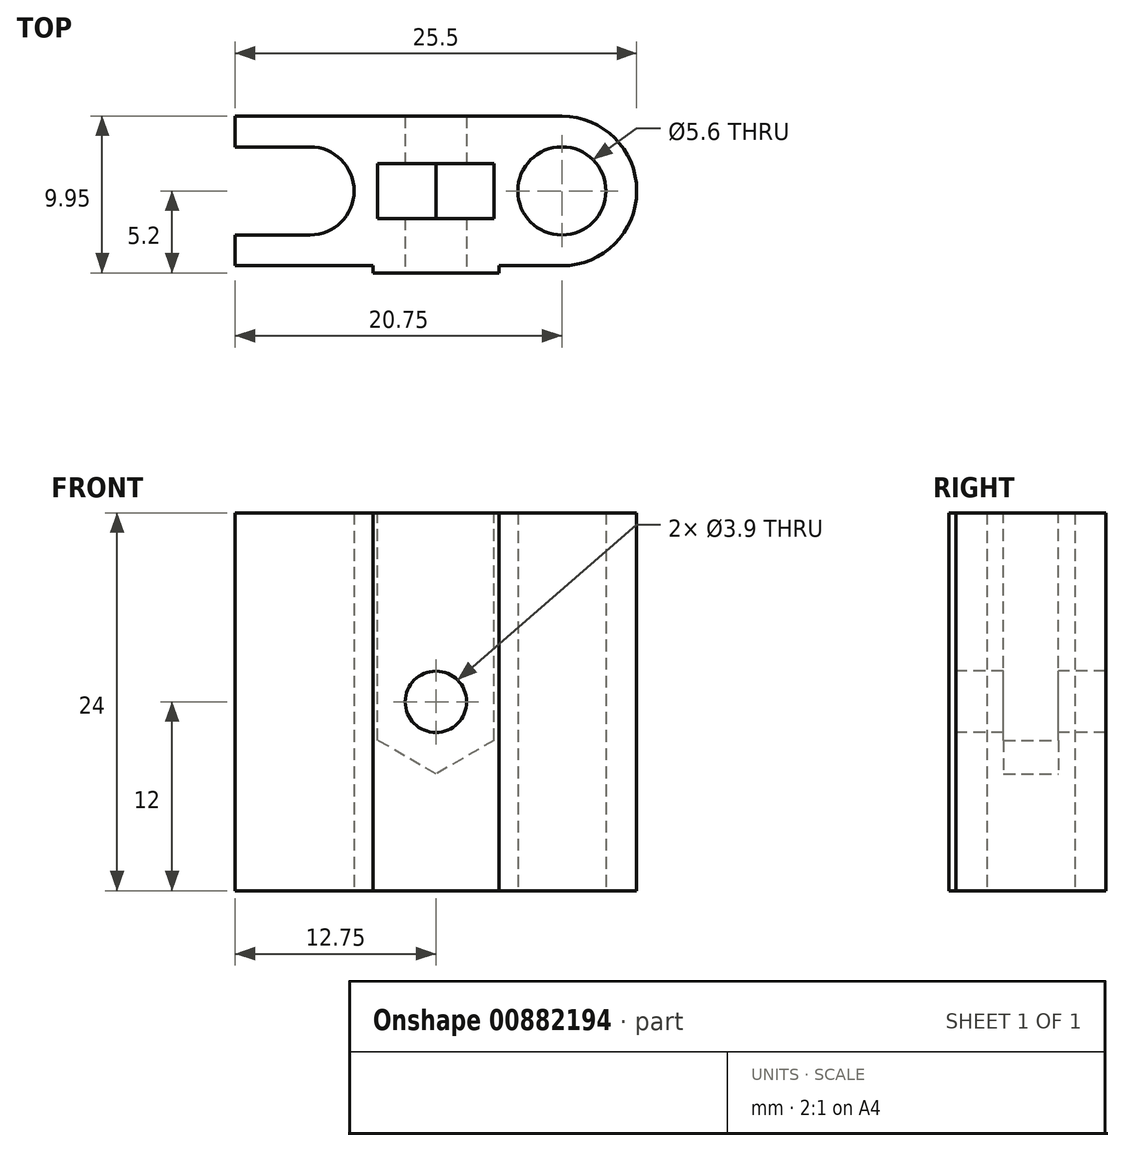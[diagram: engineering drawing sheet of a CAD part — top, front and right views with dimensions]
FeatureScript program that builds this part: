
annotation { "Feature Type Name" : "Feature", "Feature Type Description" : "" }
export const myFeature = defineFeature(function(context is Context, id is Id, definition is map)
    precondition{}
    {
        {
            var Q0;
            Q0=qCreatedBy(makeId("Top.planeOp"),FACE);
            var sketch = newSketch(context, id + "F0", { "sketchPlane" : qUnion([Q0])});
            skLineSegment(sketch, "E0", {"start": v(-8, 0) * mm, "end": v(8, 0) * mm, "construction": true});
            skArc(sketch, "E1", {"start": v(-8, -2.8) * mm, "mid": v(-5.2, 0) * mm, "end": v(-8, 2.8) * mm});
            skLineSegment(sketch, "E2", {"start": v(0, 21.05) * mm, "end": v(0, -24.42) * mm, "construction": true});
            skCircle(sketch, "E3.MirrorC", {"center": v(8, 0) * mm, "radius": 2.8 * mm});
            skLineSegment(sketch, "E4.bottom", {"start": v(8, 4.75) * mm, "end": v(-8, 4.75) * mm});
            skLineSegment(sketch, "E4.top", {"start": v(8, -4.75) * mm, "end": v(-8, -4.75) * mm});
            skLineSegment(sketch, "E4.left", {"start": v(8, 4.75) * mm, "end": v(8, -4.75) * mm, "construction": true});
            skPoint(sketch, "E4.middle", {"position": v(0, 0) * mm});
            skArc(sketch, "E5.0", {"start": v(8, 4.75) * mm, "mid": v(12.75, 0) * mm, "end": v(8, -4.75) * mm});
            skLineSegment(sketch, "E6.bottom", {"start": v(-8, 4.75) * mm, "end": v(-12.75, 4.75) * mm});
            skLineSegment(sketch, "E6.top", {"start": v(-8, -4.75) * mm, "end": v(-12.75, -4.75) * mm});
            skLineSegment(sketch, "E6.left", {"start": v(-8, 4.75) * mm, "end": v(-8, -4.75) * mm, "construction": true});
            skLineSegment(sketch, "E6.right", {"start": v(-12.75, 4.75) * mm, "end": v(-12.75, 2.8) * mm});
            skLineSegment(sketch, "E7", {"start": v(-8, 2.8) * mm, "end": v(-12.75, 2.8) * mm});
            skLineSegment(sketch, "E8", {"start": v(-8, -2.8) * mm, "end": v(-12.75, -2.8) * mm});
            skLineSegment(sketch, "E9.trimOffspring", {"start": v(-12.75, -2.8) * mm, "end": v(-12.75, -4.75) * mm});
            skLineSegment(sketch, "E10.bottom", {"start": v(4, -4.3) * mm, "end": v(-4, -4.3) * mm});
            skLineSegment(sketch, "E10.top", {"start": v(4, -5.2) * mm, "end": v(-4, -5.2) * mm});
            skLineSegment(sketch, "E10.left", {"start": v(4, -4.3) * mm, "end": v(4, -5.2) * mm});
            skLineSegment(sketch, "E10.right", {"start": v(-4, -4.3) * mm, "end": v(-4, -5.2) * mm});
            skPoint(sketch, "E10.middle", {"position": v(0, -4.75) * mm});
            skSolve(sketch);
        }
        {
            var Q0;
            Q0=qSketchRegion(id+"F0",true);
            var Q1;
            Q1=qSketchRegion(id+"F2",true);
            extrude(context, id + "F1", {"entities" : qUnion([Q0, Q1]), "depth" : 24 * mm, "offsetDistance" : 25 * mm});
        }
        {
            var Q0;
            Q0=makeQuery(id+"F1.opExtrude","SWEPT_FACE",FACE,{"disambiguationData":[OSD([sQuery(id+"F0.wireOp",EDGE,"E10.top")])]});
            var sketch = newSketch(context, id + "F2", { "sketchPlane" : qUnion([Q0])});
            skLineSegment(sketch, "E11.bottom", {"start": v(-4, 24) * mm, "end": v(4, 24) * mm, "construction": true});
            skLineSegment(sketch, "E11.top", {"start": v(-4, 0) * mm, "end": v(4, 0) * mm, "construction": true});
            skLineSegment(sketch, "E11.left", {"start": v(-4, 24) * mm, "end": v(-4, 0) * mm, "construction": true});
            skLineSegment(sketch, "E11.right", {"start": v(4, 24) * mm, "end": v(4, 0) * mm, "construction": true});
            skLineSegment(sketch, "E12", {"start": v(-4, 24) * mm, "end": v(4, 0) * mm, "construction": true});
            skLineSegment(sketch, "E13", {"start": v(0, 0) * mm, "end": v(0, 24) * mm, "construction": true});
            skCircle(sketch, "E14", {"center": v(0, 12) * mm, "radius": 1.95 * mm});
            skSolve(sketch);
        }
        {
            var Q0;
            Q0=qSketchRegion(id+"F2",true);
            extrude(context, id + "F3", {"entities" : qUnion([Q0]), "operationType" : NewBodyOperationType.REMOVE, "endBound" : BoundingType.THROUGH_ALL, "oppositeDirection" : true, "depth" : 25 * mm, "offsetDistance" : 25 * mm});
        }
        {
            var Q0;
            Q0=makeQuery(id+"F1.opExtrude","CAP_FACE",FACE,{"disambiguationData":[OSD([sQuery(id+"F0.wireOp",EDGE,"E1"),sQuery(id+"F0.wireOp",EDGE,"E3.MirrorC"),sQuery(id+"F0.wireOp",EDGE,"E4.bottom"),sQuery(id+"F0.wireOp",EDGE,"E4.top"),sQuery(id+"F0.wireOp",EDGE,"E5.0"),sQuery(id+"F0.wireOp",EDGE,"E6.bottom"),sQuery(id+"F0.wireOp",EDGE,"E6.top"),sQuery(id+"F0.wireOp",EDGE,"E6.right"),sQuery(id+"F0.wireOp",EDGE,"E7"),sQuery(id+"F0.wireOp",EDGE,"E8"),sQuery(id+"F0.wireOp",EDGE,"E9.trimOffspring"),sQuery(id+"F0.wireOp",EDGE,"E10.top"),sQuery(id+"F0.wireOp",EDGE,"E10.left"),sQuery(id+"F0.wireOp",EDGE,"E10.right")])],"isStart":false});
            var sketch = newSketch(context, id + "F4", { "sketchPlane" : qUnion([Q0])});
            skLineSegment(sketch, "E15.bottom", {"start": v(-3.7, -1.75) * mm, "end": v(3.7, -1.75) * mm});
            skLineSegment(sketch, "E15.top", {"start": v(-3.7, 1.75) * mm, "end": v(3.7, 1.75) * mm});
            skLineSegment(sketch, "E15.left", {"start": v(-3.7, -1.75) * mm, "end": v(-3.7, 1.75) * mm});
            skLineSegment(sketch, "E15.right", {"start": v(3.7, -1.75) * mm, "end": v(3.7, 1.75) * mm});
            skPoint(sketch, "E15.middle", {"position": v(0, 0) * mm});
            skSolve(sketch);
        }
        {
            var Q0;
            Q0=makeQuery(id+"F4.imprint","IMPRINT",FACE,{"disambiguationData":[TD([[makeQuery(id+"F4.imprint","IMPRINT",EDGE,{"derivedFrom":sQuery(id+"F4.wireOp",EDGE,"E15.bottom")}),1.0]])]});
            extrude(context, id + "F5", {"entities" : qUnion([Q0]), "operationType" : NewBodyOperationType.REMOVE, "oppositeDirection" : true, "depth" : 12 * mm, "offsetDistance" : 25 * mm});
        }
        {
            var Q0;
            Q0=makeQuery(id+"F5.boolean.opBoolean","COPY",FACE,{"derivedFrom":makeQuery(id+"F5.opExtrude","SWEPT_FACE",FACE,{"disambiguationData":[OSD([sQuery(id+"F4.wireOp",EDGE,"E15.top")])]})});
            var sketch = newSketch(context, id + "F6", { "sketchPlane" : qUnion([Q0])});
            skLineSegment(sketch, "E16.bottom", {"start": v(-3.7, 24) * mm, "end": v(3.7, 24) * mm, "construction": true});
            skLineSegment(sketch, "E16.top", {"start": v(-3.7, 12) * mm, "end": v(3.7, 12) * mm, "construction": true});
            skLineSegment(sketch, "E16.left", {"start": v(-3.7, 24) * mm, "end": v(-3.7, 12) * mm, "construction": true});
            skLineSegment(sketch, "E16.right", {"start": v(3.7, 24) * mm, "end": v(3.7, 12) * mm, "construction": true});
            skLineSegment(sketch, "E17", {"start": v(-3.7, 11.7) * mm, "end": v(3.7, 11.7) * mm, "construction": true});
            skCircle(sketch, "E18.cCircle", {"center": v(0, 11.7) * mm, "radius": 3.7 * mm, "construction": true});
            skLineSegment(sketch, "E18.0", {"start": v(3.7, 13.84) * mm, "end": v(3.7, 9.56) * mm});
            skLineSegment(sketch, "E18.1", {"start": v(3.7, 9.56) * mm, "end": v(0, 7.43) * mm});
            skLineSegment(sketch, "E18.2", {"start": v(0, 7.43) * mm, "end": v(-3.7, 9.56) * mm});
            skLineSegment(sketch, "E18.3", {"start": v(-3.7, 9.56) * mm, "end": v(-3.7, 13.84) * mm});
            skLineSegment(sketch, "E18.4", {"start": v(-3.7, 13.84) * mm, "end": v(0, 15.97) * mm});
            skLineSegment(sketch, "E18.5", {"start": v(0, 15.97) * mm, "end": v(3.7, 13.84) * mm});
            skPoint(sketch, "E18.0.midPoint", {"position": v(3.7, 11.7) * mm});
            skSolve(sketch);
        }
        {
            var Q0;
            Q0=qSketchRegion(id+"F6",true);
            var Q1;
            {var subQ0=sQuery(id+"F4.wireOp",EDGE,"E15.bottom");Q1=makeQuery(id+"F5.boolean.opBoolean","INTERSECT",VERTEX,{"disambiguationData":[OD(1.0)],"derivedFrom":[makeQuery(id+"F3.boolean.opBoolean","COPY",FACE,{"derivedFrom":makeQuery(id+"F3.opExtrude","SWEPT_FACE",FACE,{"disambiguationData":[OSD([sQuery(id+"F2.wireOp",EDGE,"E14")])]})}),makeQuery(id+"F5.opExtrude","SWEPT_FACE",FACE,{"disambiguationData":[OSD([subQ0])]}),makeQuery(id+"F5.opExtrude","CAP_FACE",FACE,{"disambiguationData":[OSD([subQ0,sQuery(id+"F4.wireOp",EDGE,"E15.top"),sQuery(id+"F4.wireOp",EDGE,"E15.left"),sQuery(id+"F4.wireOp",EDGE,"E15.right")])],"isStart":false})]});}
            extrude(context, id + "F7", {"entities" : qUnion([Q0]), "operationType" : NewBodyOperationType.REMOVE, "endBound" : BoundingType.UP_TO_VERTEX, "depth" : 25 * mm, "endBoundEntityVertex" : qUnion([Q1]), "offsetDistance" : 25 * mm});
        }
    });
